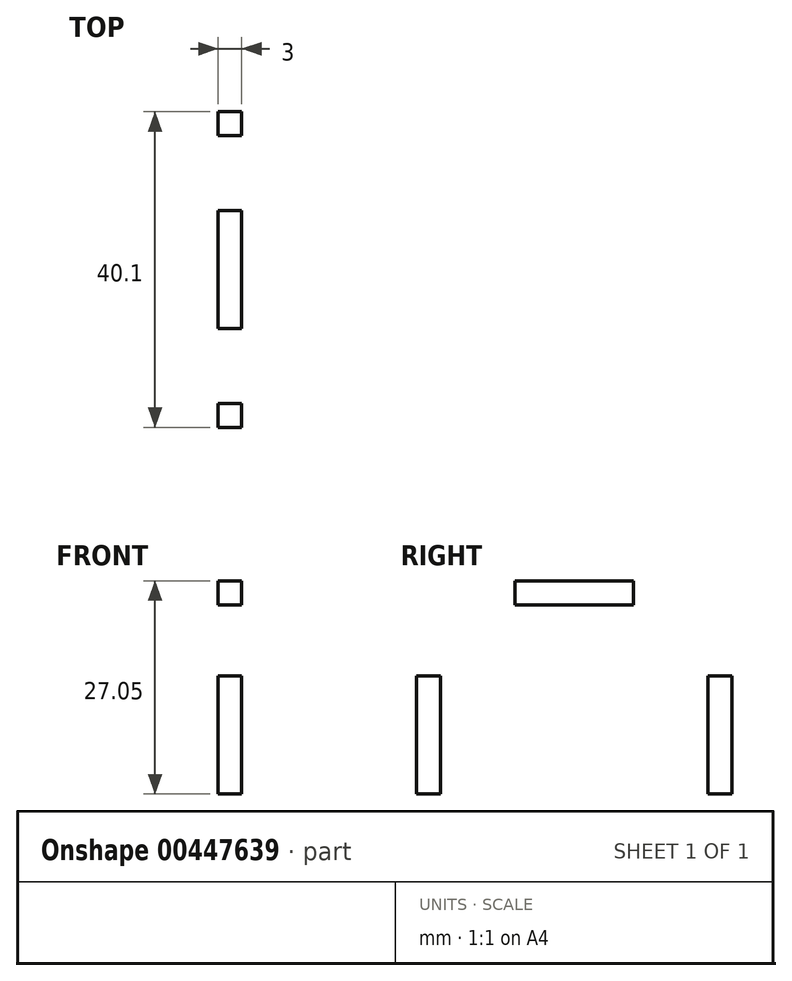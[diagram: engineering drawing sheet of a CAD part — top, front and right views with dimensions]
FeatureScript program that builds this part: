
annotation { "Feature Type Name" : "Feature", "Feature Type Description" : "" }
export const myFeature = defineFeature(function(context is Context, id is Id, definition is map)
    precondition{}
    {
        {
            var Q0;
            Q0=qCreatedBy(makeId("Right.planeOp"),FACE);
            var sketch = newSketch(context, id + "F0", { "sketchPlane" : qUnion([Q0])});
            skLineSegment(sketch, "E0.bottom", {"start": v(17, 16.5) * mm, "end": v(-17, 16.5) * mm});
            skLineSegment(sketch, "E0.top", {"start": v(17, -16.5) * mm, "end": v(-17, -16.5) * mm});
            skLineSegment(sketch, "E0.left", {"start": v(17, 16.5) * mm, "end": v(17, -16.5) * mm});
            skLineSegment(sketch, "E0.right", {"start": v(-17, 16.5) * mm, "end": v(-17, -16.5) * mm});
            skPoint(sketch, "E0.middle", {"position": v(0, 0) * mm});
            skLineSegment(sketch, "E1.bottom", {"start": v(7.5, 19.55) * mm, "end": v(-7.5, 19.55) * mm});
            skLineSegment(sketch, "E1.top", {"start": v(7.5, 16.5) * mm, "end": v(-7.5, 16.5) * mm});
            skLineSegment(sketch, "E1.left", {"start": v(7.5, 19.55) * mm, "end": v(7.5, 16.5) * mm});
            skLineSegment(sketch, "E1.right", {"start": v(-7.5, 19.55) * mm, "end": v(-7.5, 16.5) * mm});
            skPoint(sketch, "E1.middle", {"position": v(0, 18.03) * mm});
            skLineSegment(sketch, "E2.bottom", {"start": v(4.95, 3.5) * mm, "end": v(-4.95, 3.5) * mm});
            skLineSegment(sketch, "E2.top", {"start": v(4.95, 6.5) * mm, "end": v(-4.95, 6.5) * mm});
            skLineSegment(sketch, "E2.left", {"start": v(4.95, 3.5) * mm, "end": v(4.95, 6.5) * mm});
            skLineSegment(sketch, "E2.right", {"start": v(-4.95, 3.5) * mm, "end": v(-4.95, 6.5) * mm});
            skLineSegment(sketch, "E3.top", {"start": v(7.45, -13.45) * mm, "end": v(-7.45, -13.45) * mm});
            skLineSegment(sketch, "E3.left", {"start": v(7.45, -16.5) * mm, "end": v(7.45, -13.45) * mm});
            skLineSegment(sketch, "E3.right", {"start": v(-7.45, -16.5) * mm, "end": v(-7.45, -13.45) * mm});
            skPoint(sketch, "E3.middle", {"position": v(0, -14.97) * mm});
            skLineSegment(sketch, "E4.bottom", {"start": v(-20.05, -7.5) * mm, "end": v(-17, -7.5) * mm});
            skLineSegment(sketch, "E4.top", {"start": v(-20.05, 7.5) * mm, "end": v(-17, 7.5) * mm});
            skLineSegment(sketch, "E4.left", {"start": v(-20.05, -7.5) * mm, "end": v(-20.05, 7.5) * mm});
            skLineSegment(sketch, "E4.right", {"start": v(-17, -7.5) * mm, "end": v(-17, 7.5) * mm});
            skPoint(sketch, "E4.middle", {"position": v(-18.52, 0) * mm});
            skLineSegment(sketch, "E5.bottom", {"start": v(20.05, -7.5) * mm, "end": v(17, -7.5) * mm});
            skLineSegment(sketch, "E5.top", {"start": v(20.05, 7.5) * mm, "end": v(17, 7.5) * mm});
            skLineSegment(sketch, "E5.left", {"start": v(20.05, -7.5) * mm, "end": v(20.05, 7.5) * mm});
            skLineSegment(sketch, "E5.right", {"start": v(17, -7.5) * mm, "end": v(17, 7.5) * mm});
            skPoint(sketch, "E5.middle", {"position": v(18.52, 0) * mm});
            skCircle(sketch, "E6", {"center": v(0, -5.97) * mm, "radius": 5.5 * mm});
            skSolve(sketch);
        }
        {
            var Q0;
            {var subQ0=sQuery(id+"F0.wireOp",EDGE,"E1.top");Q0=makeQuery(id+"F0.imprint","IMPRINT",FACE,{"disambiguationData":[TD([[makeQuery(id+"F0.imprint","IMPRINT",EDGE,{"derivedFrom":subQ0}),1.0]])]});}
            var Q1;
            Q1=makeQuery(id+"F0.imprint","IMPRINT",FACE,{"disambiguationData":[TD([[makeQuery(id+"F0.imprint","IMPRINT",EDGE,{"derivedFrom":sQuery(id+"F0.wireOp",EDGE,"E1.bottom")}),1.0]])]});
            var Q2;
            Q2=makeQuery(id+"F0.imprint","IMPRINT",FACE,{"disambiguationData":[TD([[makeQuery(id+"F0.imprint","IMPRINT",EDGE,{"derivedFrom":sQuery(id+"F0.wireOp",EDGE,"E4.bottom")}),1.0]])]});
            var Q3;
            Q3=makeQuery(id+"F0.imprint","IMPRINT",FACE,{"disambiguationData":[TD([[makeQuery(id+"F0.imprint","IMPRINT",EDGE,{"derivedFrom":sQuery(id+"F0.wireOp",EDGE,"E5.bottom")}),-1.0]])]});
            extrude(context, id + "F1", {"entities" : qUnion([Q0, Q1, Q2, Q3]), "depth" : 3 * mm});
        }
    });
